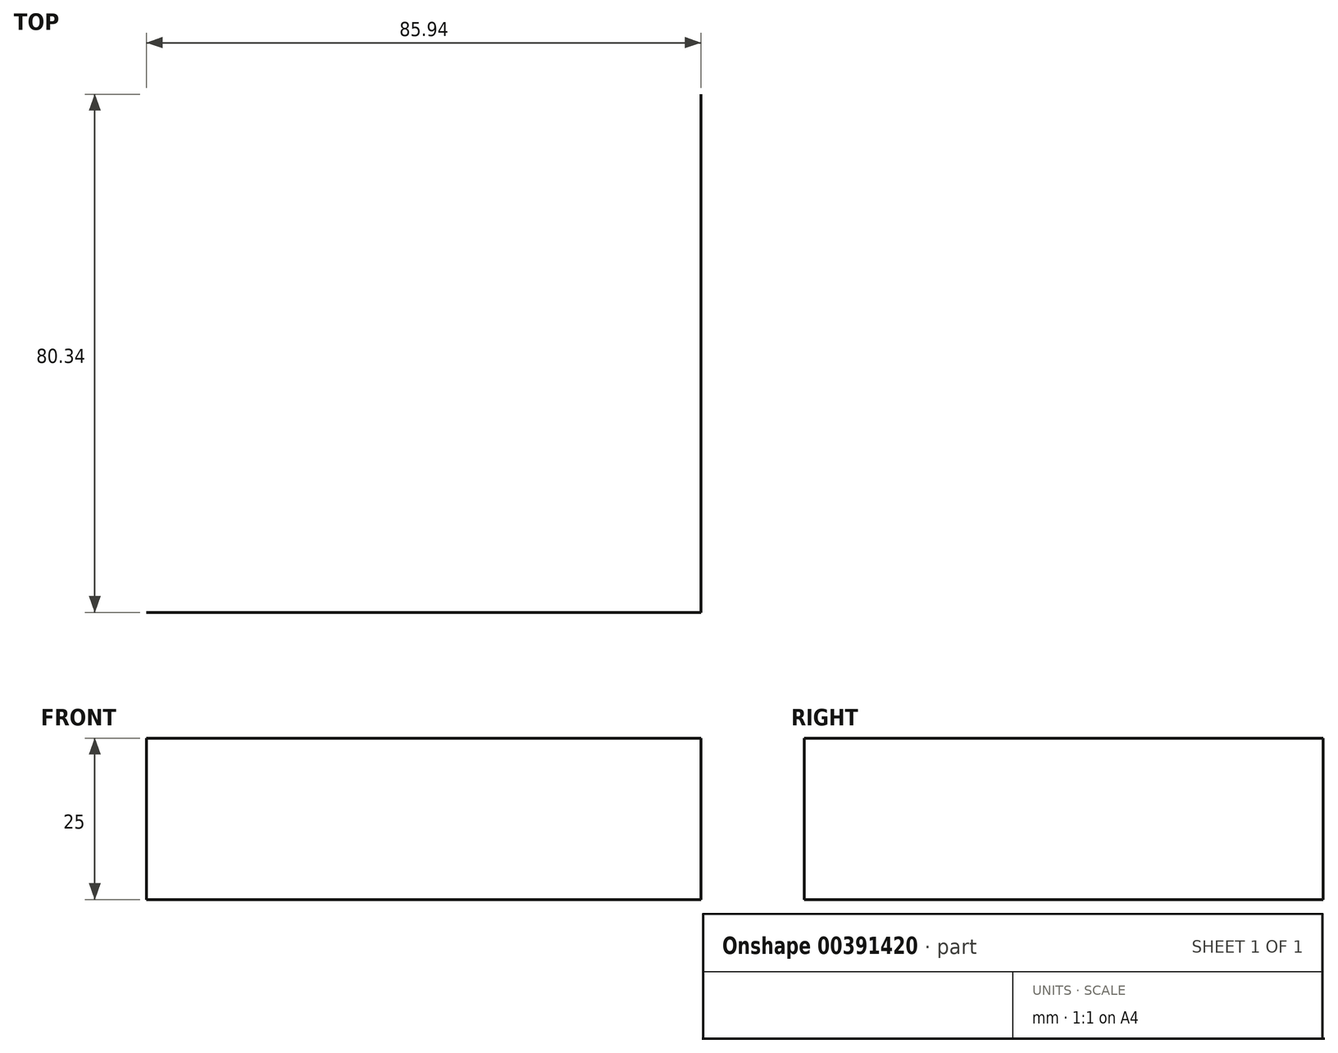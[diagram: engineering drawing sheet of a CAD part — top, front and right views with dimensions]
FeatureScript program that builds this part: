
annotation { "Feature Type Name" : "Feature", "Feature Type Description" : "" }
export const myFeature = defineFeature(function(context is Context, id is Id, definition is map)
    precondition{}
    {
        {
            var Q0;
            Q0=qCreatedBy(makeId("Top.planeOp"),FACE);
            var sketch = newSketch(context, id + "F0", { "sketchPlane" : qUnion([Q0])});
            skLineSegment(sketch, "E0.bottom", {"start": v(-42.97, -40.17) * mm, "end": v(42.97, -40.17) * mm});
            skLineSegment(sketch, "E0.top", {"start": v(-42.97, 40.17) * mm, "end": v(42.97, 40.17) * mm});
            skLineSegment(sketch, "E0.left", {"start": v(-42.97, -40.17) * mm, "end": v(-42.97, 40.17) * mm});
            skLineSegment(sketch, "E0.right", {"start": v(42.97, -40.17) * mm, "end": v(42.97, 40.17) * mm});
            skPoint(sketch, "E0.middle", {"position": v(0, 0) * mm});
            skSolve(sketch);
        }
        {
            var Q0;
            Q0=sQuery(id+"F0.wireOp",EDGE,"E0.right");
            var Q1;
            Q1=sQuery(id+"F0.wireOp",EDGE,"E0.bottom");
            extrude(context, id + "F1", {"bodyType" : ToolBodyType.SURFACE, "surfaceEntities" : qUnion([Q0, Q1]), "depth" : 25 * mm});
        }
    });
